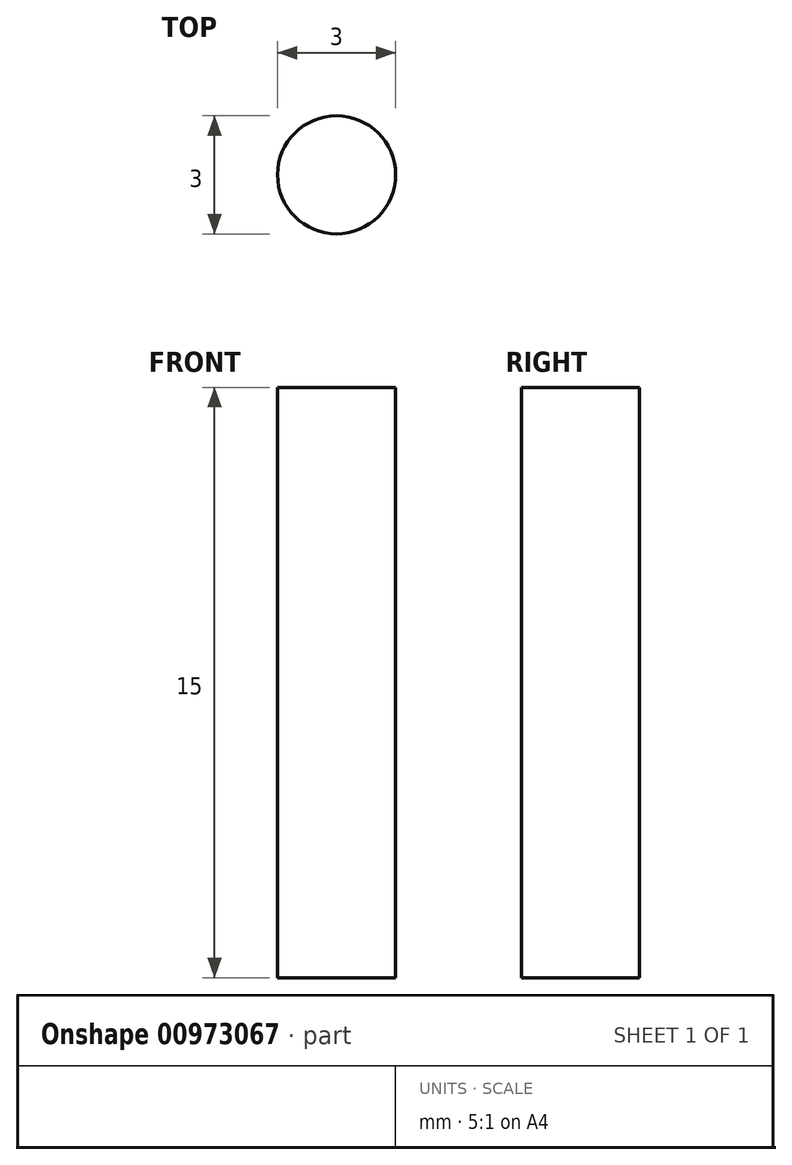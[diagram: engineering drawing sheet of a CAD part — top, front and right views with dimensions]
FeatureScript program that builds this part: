
annotation { "Feature Type Name" : "Feature", "Feature Type Description" : "" }
export const myFeature = defineFeature(function(context is Context, id is Id, definition is map)
    precondition{}
    {
        {
            var Q0;
            Q0=qCreatedBy(makeId("Top.planeOp"),FACE);
            var sketch = newSketch(context, id + "F0", { "sketchPlane" : qUnion([Q0])});
            skCircle(sketch, "E0", {"center": v(0, 0) * mm, "radius": 1.5 * mm});
            skSolve(sketch);
        }
        {
            var Q0;
            Q0 = qSketchRegion(id + "F0", true);
            extrude(context, id + "F1", {"entities" : qUnion([Q0]), "depth" : 15 * mm, "offsetDistance" : 25 * mm});
        }
    });
